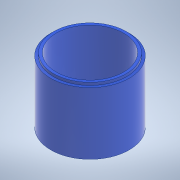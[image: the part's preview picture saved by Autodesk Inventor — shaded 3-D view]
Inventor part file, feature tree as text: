
AUTODESK INVENTOR PART (.ipt)
format: ipt  version: 2020 (Build 240168000, 168)  size: 130,048 bytes
history: native  units: mm
features: extrude x2, sketch x1
ambient origin geometry x8: Origin, YZ Plane, XZ Plane, XY Plane, X Axis, Y Axis, Z Axis, Center Point
bodies: Solid1 (feature_tree)
feature tree (3):
  sketch  "Sketch1"  dims[d0=50.0mm d1=54.0mm d2=58.0mm d3=46.0mm d4=0.0mm d5=44.0mm d6=2.0mm d7=0.0mm d8=0.0mm]
  extrude  "Extrusion1"  Depth=2.0mm
  extrude  "Extrusion2"  Depth=2.0mm
